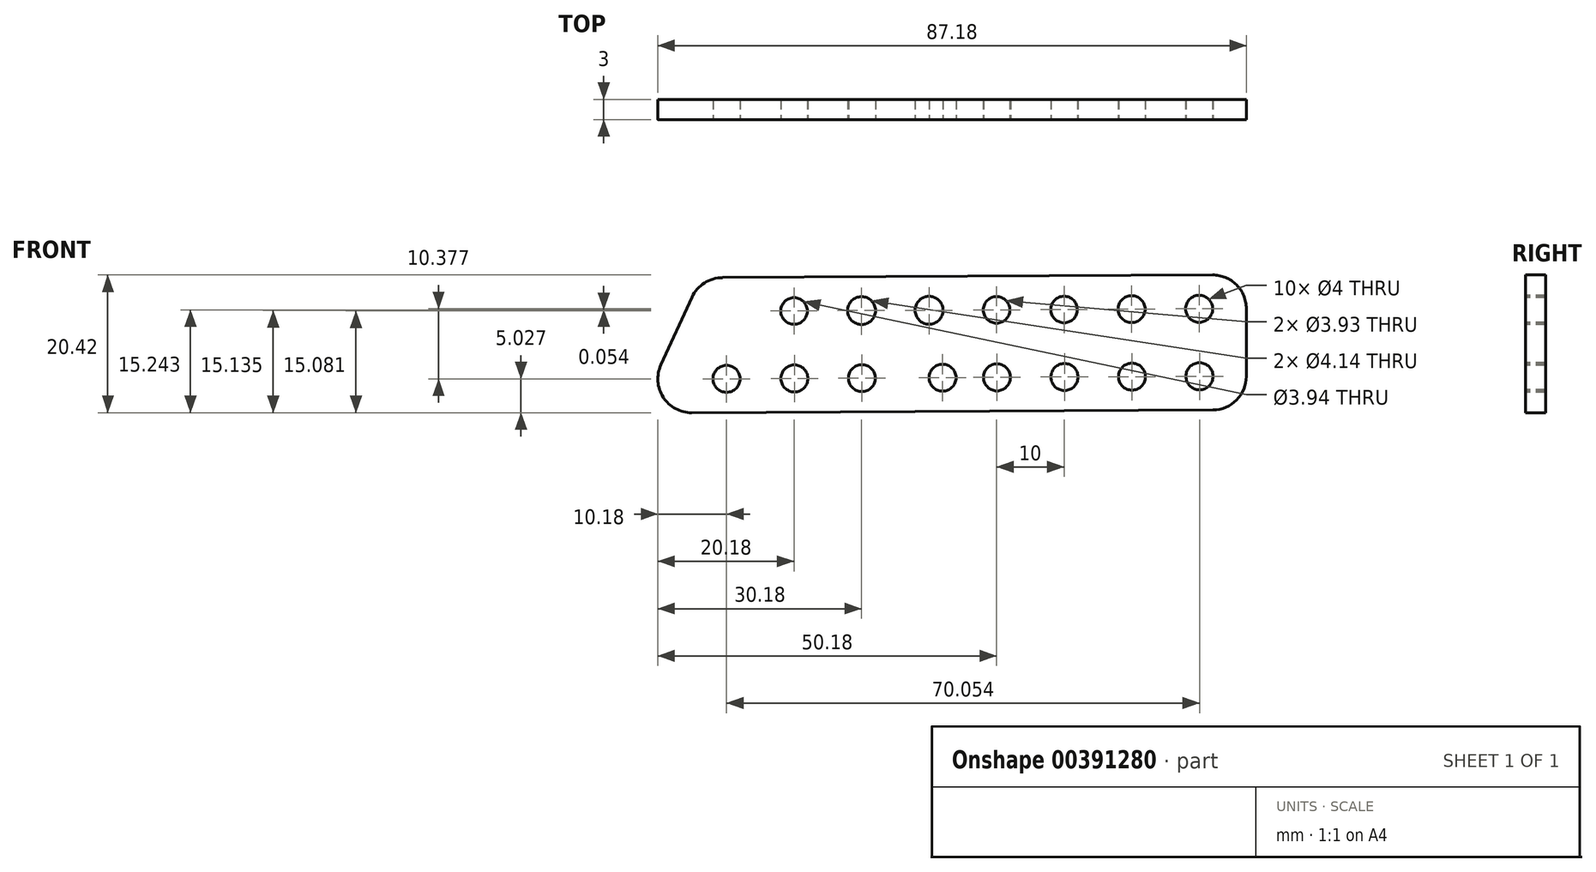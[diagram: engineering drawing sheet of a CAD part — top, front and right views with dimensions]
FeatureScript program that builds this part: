
annotation { "Feature Type Name" : "Feature", "Feature Type Description" : "" }
export const myFeature = defineFeature(function(context is Context, id is Id, definition is map)
    precondition{}
    {
        {
            var Q0;
            Q0=qCreatedBy(makeId("Front.planeOp"),FACE);
            var sketch = newSketch(context, id + "F0", { "sketchPlane" : qUnion([Q0])});
            skLineSegment(sketch, "E0.bottom", {"start": v(45, -9.76) * mm, "end": v(-45, -10.24) * mm});
            skLineSegment(sketch, "E0.left", {"start": v(45, -9.76) * mm, "end": v(45, 10.24) * mm});
            skPoint(sketch, "E0.middle", {"position": v(0, 0) * mm});
            skLineSegment(sketch, "E1", {"start": v(-45, -10.24) * mm, "end": v(-35.78, 9.8) * mm});
            skLineSegment(sketch, "E2", {"start": v(45, 10.24) * mm, "end": v(-35.78, 9.8) * mm});
            skSolve(sketch);
        }
        {
            var Q0;
            Q0 = qSketchRegion(id + "F0", true);
            extrude(context, id + "F1", {"entities" : qUnion([Q0]), "endBound" : BoundingType.SYMMETRIC, "depth" : 3 * mm});
        }
        {
            var Q0;
            Q0=makeQuery(id+"F1.opExtrude","SWEPT_EDGE",EDGE,{"disambiguationData":[OSD([sQuery(id+"F0.wireOp",EDGE,"E0.top"),sQuery(id+"F0.wireOp",EDGE,"E0.right")])]});
            var Q1;
            Q1=makeQuery(id+"F1.opExtrude","SWEPT_EDGE",EDGE,{"disambiguationData":[OSD([sQuery(id+"F0.wireOp",EDGE,"E0.bottom"),sQuery(id+"F0.wireOp",EDGE,"E0.right")])]});
            var Q2;
            Q2=makeQuery(id+"F1.opExtrude","SWEPT_EDGE",EDGE,{"disambiguationData":[OSD([sQuery(id+"F0.wireOp",EDGE,"E0.bottom"),sQuery(id+"F0.wireOp",EDGE,"E0.left")])]});
            var Q3;
            Q3=makeQuery(id+"F1.opExtrude","SWEPT_EDGE",EDGE,{"disambiguationData":[OSD([sQuery(id+"F0.wireOp",EDGE,"E0.top"),sQuery(id+"F0.wireOp",EDGE,"E0.left")])]});
            var Q4;
            Q4=makeQuery(id+"F1.opExtrude","SWEPT_EDGE",EDGE,{"disambiguationData":[OSD([sQuery(id+"F0.wireOp",EDGE,"E1"),sQuery(id+"F0.wireOp",EDGE,"E2")])]});
            fillet(context, id + "F2", {"entities" : qUnion([Q0, Q1, Q2, Q3, Q4]), "radius" : 5 * mm, "tangentPropagation" : true, "allowEdgeOverflow" : false});
        }
        {
            var Q0;
            Q0=makeQuery(id+"F1.opExtrude","CAP_FACE",FACE,{"disambiguationData":[OSD([sQuery(id+"F0.wireOp",EDGE,"E0.bottom"),sQuery(id+"F0.wireOp",EDGE,"E0.left"),sQuery(id+"F0.wireOp",EDGE,"E1"),sQuery(id+"F0.wireOp",EDGE,"E2")])],"isStart":false});
            var sketch = newSketch(context, id + "F3", { "sketchPlane" : qUnion([Q0])});
            skCircle(sketch, "E3", {"center": v(38, 5.2) * mm, "radius": 2 * mm});
            skLineSegment(sketch, "E4", {"start": v(38, 5.2) * mm, "end": v(-26.94, 4.85) * mm, "construction": true});
            skCircle(sketch, "E5", {"center": v(28, 5.15) * mm, "radius": 2 * mm});
            skCircle(sketch, "E6", {"center": v(18, 5.1) * mm, "radius": 1.97 * mm});
            skCircle(sketch, "E7", {"center": v(8, 5.04) * mm, "radius": 1.97 * mm});
            skCircle(sketch, "E8", {"center": v(-2, 4.99) * mm, "radius": 2.07 * mm});
            skCircle(sketch, "E9", {"center": v(-12, 4.94) * mm, "radius": 2.07 * mm});
            skCircle(sketch, "E10", {"center": v(-22, 4.88) * mm, "radius": 1.97 * mm});
            skLineSegment(sketch, "E11", {"start": v(38, 5.2) * mm, "end": v(38.05, -4.8) * mm, "construction": true});
            skLineSegment(sketch, "E12", {"start": v(38.05, -4.8) * mm, "end": v(-37.94, -5.2) * mm, "construction": true});
            skLineSegment(sketch, "E13", {"start": v(28, 5.15) * mm, "end": v(28.05, -4.85) * mm, "construction": true});
            skLineSegment(sketch, "E14", {"start": v(18, 5.1) * mm, "end": v(18.05, -4.9) * mm, "construction": true});
            skLineSegment(sketch, "E15", {"start": v(8, 5.04) * mm, "end": v(8.05, -4.96) * mm, "construction": true});
            skLineSegment(sketch, "E16", {"start": v(-2, 4.99) * mm, "end": v(0, -5) * mm, "construction": true});
            skLineSegment(sketch, "E17", {"start": v(-12, 4.94) * mm, "end": v(-11.95, -5.06) * mm, "construction": true});
            skLineSegment(sketch, "E18", {"start": v(-22, 4.88) * mm, "end": v(-21.95, -5.12) * mm, "construction": true});
            skCircle(sketch, "E19", {"center": v(38.05, -4.8) * mm, "radius": 2 * mm});
            skCircle(sketch, "E20", {"center": v(28.05, -4.85) * mm, "radius": 2 * mm});
            skCircle(sketch, "E21", {"center": v(18.05, -4.9) * mm, "radius": 2 * mm});
            skCircle(sketch, "E22", {"center": v(8.05, -4.96) * mm, "radius": 2 * mm});
            skCircle(sketch, "E23", {"center": v(0, -5) * mm, "radius": 2 * mm});
            skCircle(sketch, "E24", {"center": v(-11.95, -5.06) * mm, "radius": 2 * mm});
            skCircle(sketch, "E25", {"center": v(-21.95, -5.12) * mm, "radius": 2 * mm});
            skCircle(sketch, "E26", {"center": v(-32, -5.17) * mm, "radius": 2 * mm});
            skSolve(sketch);
        }
        {
            var Q0;
            Q0 = qSketchRegion(id + "F3", true);
            extrude(context, id + "F4", {"entities" : qUnion([Q0]), "operationType" : NewBodyOperationType.REMOVE, "oppositeDirection" : true, "depth" : 25 * mm});
        }
    });
